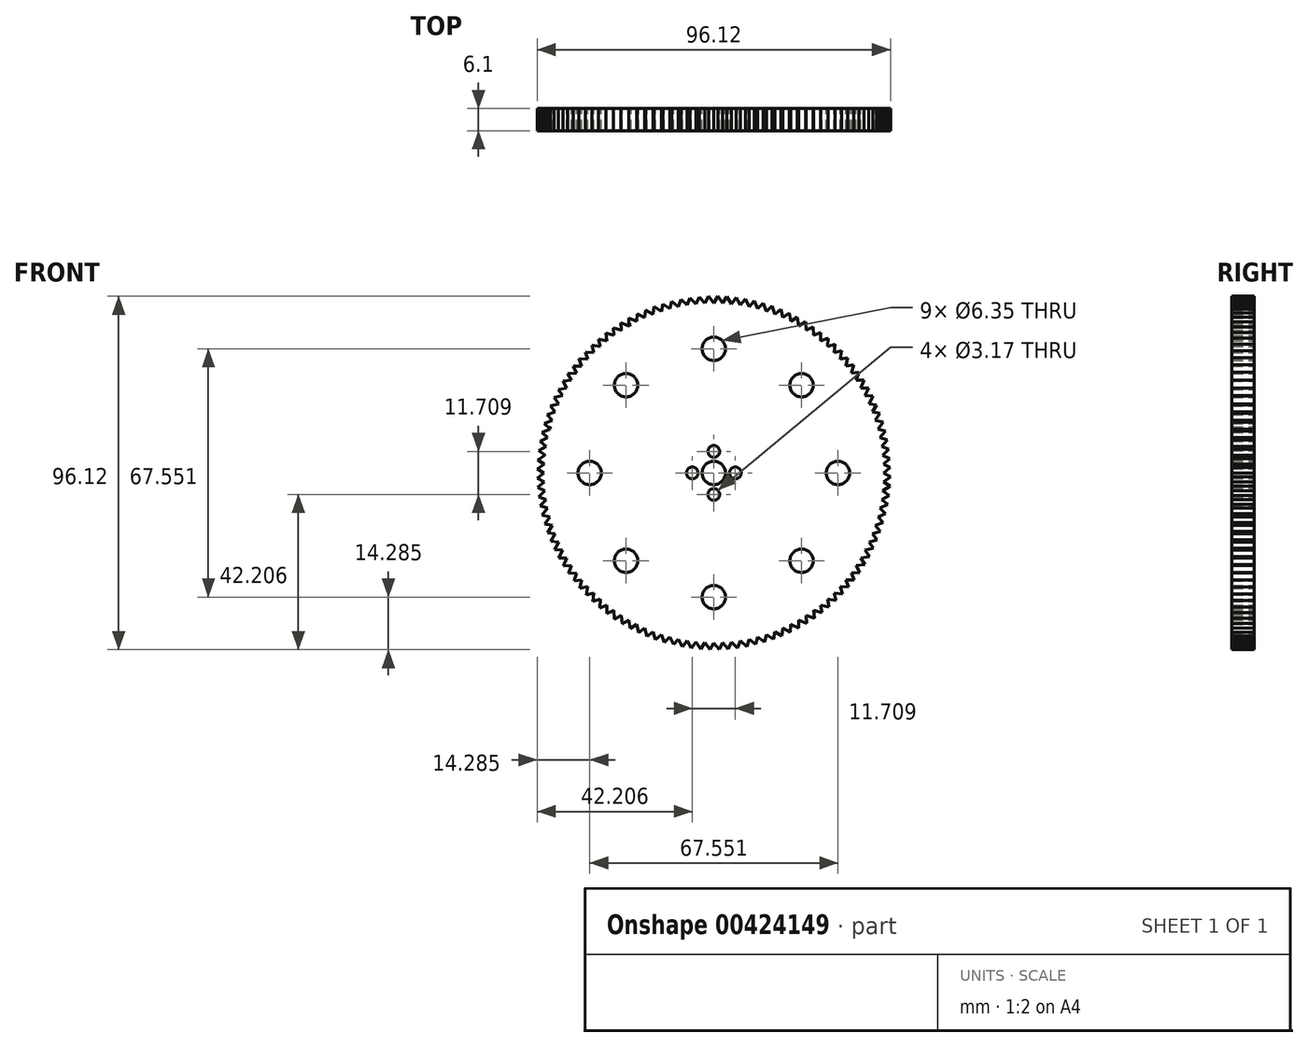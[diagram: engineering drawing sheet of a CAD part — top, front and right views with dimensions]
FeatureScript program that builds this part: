
annotation { "Feature Type Name" : "Feature", "Feature Type Description" : "" }
export const myFeature = defineFeature(function(context is Context, id is Id, definition is map)
    precondition{}
    {
        {
            var Q0;
            Q0=qCreatedBy(makeId("Front.planeOp"),FACE);
            var sketch = newSketch(context, id + "F0", { "sketchPlane" : qUnion([Q0])});
            skCircle(sketch, "E0", {"center": v(0, 0) * mm, "radius": 46.23 * mm});
            skPoint(sketch, "E1", {"position": v(0, 33.78) * mm});
            skPoint(sketch, "E2.1.0", {"position": v(23.88, 23.88) * mm});
            skPoint(sketch, "E2.2.0", {"position": v(33.78, 0) * mm});
            skPoint(sketch, "E2.3.0", {"position": v(23.88, -23.88) * mm});
            skPoint(sketch, "E2.4.0", {"position": v(0, -33.78) * mm});
            skPoint(sketch, "E2.5.0", {"position": v(-23.88, -23.88) * mm});
            skPoint(sketch, "E2.6.0", {"position": v(-33.78, 0) * mm});
            skPoint(sketch, "E2.7.0", {"position": v(-23.88, 23.88) * mm});
            skLineSegment(sketch, "E2.anchor1", {"start": v(0, 0) * mm, "end": v(0, 33.78) * mm, "construction": true});
            skLineSegment(sketch, "E2.anchor2", {"start": v(0, 0) * mm, "end": v(-23.88, 23.88) * mm, "construction": true});
            skPoint(sketch, "E3", {"position": v(0, -5.85) * mm});
            skPoint(sketch, "E4.1.0", {"position": v(-5.85, 0) * mm});
            skPoint(sketch, "E4.2.0", {"position": v(0, 5.85) * mm});
            skPoint(sketch, "E4.3.0", {"position": v(5.85, 0) * mm});
            skLineSegment(sketch, "E4.anchor1", {"start": v(0, 0) * mm, "end": v(0, -5.85) * mm, "construction": true});
            skLineSegment(sketch, "E4.anchor2", {"start": v(0, 0) * mm, "end": v(5.85, 0) * mm, "construction": true});
            skPoint(sketch, "E5", {"position": v(0, -46.23) * mm});
            skPoint(sketch, "E6.1.0", {"position": v(2.42, -46.16) * mm});
            skPoint(sketch, "E6.2.0", {"position": v(4.83, -45.97) * mm});
            skPoint(sketch, "E6.3.0", {"position": v(7.23, -45.66) * mm});
            skPoint(sketch, "E6.4.0", {"position": v(9.61, -45.22) * mm});
            skPoint(sketch, "E6.5.0", {"position": v(11.96, -44.65) * mm});
            skPoint(sketch, "E6.6.0", {"position": v(14.29, -43.97) * mm});
            skPoint(sketch, "E6.7.0", {"position": v(16.57, -43.16) * mm});
            skPoint(sketch, "E6.8.0", {"position": v(18.8, -42.23) * mm});
            skPoint(sketch, "E6.9.0", {"position": v(20.99, -41.19) * mm});
            skPoint(sketch, "E6.10.0", {"position": v(23.11, -40.03) * mm});
            skPoint(sketch, "E6.11.0", {"position": v(25.18, -38.77) * mm});
            skPoint(sketch, "E6.12.0", {"position": v(27.17, -37.4) * mm});
            skPoint(sketch, "E6.13.0", {"position": v(29.1, -35.93) * mm});
            skPoint(sketch, "E6.14.0", {"position": v(30.93, -34.35) * mm});
            skPoint(sketch, "E6.15.0", {"position": v(32.69, -32.69) * mm});
            skPoint(sketch, "E6.16.0", {"position": v(34.35, -30.93) * mm});
            skPoint(sketch, "E6.17.0", {"position": v(35.93, -29.1) * mm});
            skPoint(sketch, "E6.18.0", {"position": v(37.4, -27.17) * mm});
            skPoint(sketch, "E6.19.0", {"position": v(38.77, -25.18) * mm});
            skPoint(sketch, "E6.20.0", {"position": v(40.03, -23.11) * mm});
            skPoint(sketch, "E6.21.0", {"position": v(41.19, -20.99) * mm});
            skPoint(sketch, "E6.22.0", {"position": v(42.23, -18.8) * mm});
            skPoint(sketch, "E6.23.0", {"position": v(43.16, -16.57) * mm});
            skPoint(sketch, "E6.24.0", {"position": v(43.97, -14.29) * mm});
            skPoint(sketch, "E6.25.0", {"position": v(44.65, -11.96) * mm});
            skPoint(sketch, "E6.26.0", {"position": v(45.22, -9.61) * mm});
            skPoint(sketch, "E6.27.0", {"position": v(45.66, -7.23) * mm});
            skPoint(sketch, "E6.28.0", {"position": v(45.97, -4.83) * mm});
            skPoint(sketch, "E6.29.0", {"position": v(46.16, -2.42) * mm});
            skPoint(sketch, "E6.30.0", {"position": v(46.23, 0) * mm});
            skPoint(sketch, "E6.31.0", {"position": v(46.16, 2.42) * mm});
            skPoint(sketch, "E6.32.0", {"position": v(45.97, 4.83) * mm});
            skPoint(sketch, "E6.33.0", {"position": v(45.66, 7.23) * mm});
            skPoint(sketch, "E6.34.0", {"position": v(45.22, 9.61) * mm});
            skPoint(sketch, "E6.35.0", {"position": v(44.65, 11.96) * mm});
            skPoint(sketch, "E6.36.0", {"position": v(43.97, 14.29) * mm});
            skPoint(sketch, "E6.37.0", {"position": v(43.16, 16.57) * mm});
            skPoint(sketch, "E6.38.0", {"position": v(42.23, 18.8) * mm});
            skPoint(sketch, "E6.39.0", {"position": v(41.19, 20.99) * mm});
            skPoint(sketch, "E6.40.0", {"position": v(40.03, 23.11) * mm});
            skPoint(sketch, "E6.41.0", {"position": v(38.77, 25.18) * mm});
            skPoint(sketch, "E6.42.0", {"position": v(37.4, 27.17) * mm});
            skPoint(sketch, "E6.43.0", {"position": v(35.93, 29.1) * mm});
            skPoint(sketch, "E6.44.0", {"position": v(34.35, 30.93) * mm});
            skPoint(sketch, "E6.45.0", {"position": v(32.69, 32.69) * mm});
            skPoint(sketch, "E6.46.0", {"position": v(30.93, 34.35) * mm});
            skPoint(sketch, "E6.47.0", {"position": v(29.1, 35.93) * mm});
            skPoint(sketch, "E6.48.0", {"position": v(27.17, 37.4) * mm});
            skPoint(sketch, "E6.49.0", {"position": v(25.18, 38.77) * mm});
            skPoint(sketch, "E6.50.0", {"position": v(23.11, 40.03) * mm});
            skPoint(sketch, "E6.51.0", {"position": v(20.99, 41.19) * mm});
            skPoint(sketch, "E6.52.0", {"position": v(18.8, 42.23) * mm});
            skPoint(sketch, "E6.53.0", {"position": v(16.57, 43.16) * mm});
            skPoint(sketch, "E6.54.0", {"position": v(14.29, 43.97) * mm});
            skPoint(sketch, "E6.55.0", {"position": v(11.96, 44.65) * mm});
            skPoint(sketch, "E6.56.0", {"position": v(9.61, 45.22) * mm});
            skPoint(sketch, "E6.57.0", {"position": v(7.23, 45.66) * mm});
            skPoint(sketch, "E6.58.0", {"position": v(4.83, 45.97) * mm});
            skPoint(sketch, "E6.59.0", {"position": v(2.42, 46.16) * mm});
            skPoint(sketch, "E6.60.0", {"position": v(0, 46.23) * mm});
            skPoint(sketch, "E6.61.0", {"position": v(-2.42, 46.16) * mm});
            skPoint(sketch, "E6.62.0", {"position": v(-4.83, 45.97) * mm});
            skPoint(sketch, "E6.63.0", {"position": v(-7.23, 45.66) * mm});
            skPoint(sketch, "E6.64.0", {"position": v(-9.61, 45.22) * mm});
            skPoint(sketch, "E6.65.0", {"position": v(-11.96, 44.65) * mm});
            skPoint(sketch, "E6.66.0", {"position": v(-14.29, 43.97) * mm});
            skPoint(sketch, "E6.67.0", {"position": v(-16.57, 43.16) * mm});
            skPoint(sketch, "E6.68.0", {"position": v(-18.8, 42.23) * mm});
            skPoint(sketch, "E6.69.0", {"position": v(-20.99, 41.19) * mm});
            skPoint(sketch, "E6.70.0", {"position": v(-23.11, 40.03) * mm});
            skPoint(sketch, "E6.71.0", {"position": v(-25.18, 38.77) * mm});
            skPoint(sketch, "E6.72.0", {"position": v(-27.17, 37.4) * mm});
            skPoint(sketch, "E6.73.0", {"position": v(-29.1, 35.93) * mm});
            skPoint(sketch, "E6.74.0", {"position": v(-30.93, 34.35) * mm});
            skPoint(sketch, "E6.75.0", {"position": v(-32.69, 32.69) * mm});
            skPoint(sketch, "E6.76.0", {"position": v(-34.35, 30.93) * mm});
            skPoint(sketch, "E6.77.0", {"position": v(-35.93, 29.1) * mm});
            skPoint(sketch, "E6.78.0", {"position": v(-37.4, 27.17) * mm});
            skPoint(sketch, "E6.79.0", {"position": v(-38.77, 25.18) * mm});
            skPoint(sketch, "E6.80.0", {"position": v(-40.03, 23.11) * mm});
            skPoint(sketch, "E6.81.0", {"position": v(-41.19, 20.99) * mm});
            skPoint(sketch, "E6.82.0", {"position": v(-42.23, 18.8) * mm});
            skPoint(sketch, "E6.83.0", {"position": v(-43.16, 16.57) * mm});
            skPoint(sketch, "E6.84.0", {"position": v(-43.97, 14.29) * mm});
            skPoint(sketch, "E6.85.0", {"position": v(-44.65, 11.96) * mm});
            skPoint(sketch, "E6.86.0", {"position": v(-45.22, 9.61) * mm});
            skPoint(sketch, "E6.87.0", {"position": v(-45.66, 7.23) * mm});
            skPoint(sketch, "E6.88.0", {"position": v(-45.97, 4.83) * mm});
            skPoint(sketch, "E6.89.0", {"position": v(-46.16, 2.42) * mm});
            skPoint(sketch, "E6.90.0", {"position": v(-46.23, 0) * mm});
            skPoint(sketch, "E6.91.0", {"position": v(-46.16, -2.42) * mm});
            skPoint(sketch, "E6.92.0", {"position": v(-45.97, -4.83) * mm});
            skPoint(sketch, "E6.93.0", {"position": v(-45.66, -7.23) * mm});
            skPoint(sketch, "E6.94.0", {"position": v(-45.22, -9.61) * mm});
            skPoint(sketch, "E6.95.0", {"position": v(-44.65, -11.96) * mm});
            skPoint(sketch, "E6.96.0", {"position": v(-43.97, -14.29) * mm});
            skPoint(sketch, "E6.97.0", {"position": v(-43.16, -16.57) * mm});
            skPoint(sketch, "E6.98.0", {"position": v(-42.23, -18.8) * mm});
            skPoint(sketch, "E6.99.0", {"position": v(-41.19, -20.99) * mm});
            skPoint(sketch, "E6.100.0", {"position": v(-40.03, -23.11) * mm});
            skPoint(sketch, "E6.101.0", {"position": v(-38.77, -25.18) * mm});
            skPoint(sketch, "E6.102.0", {"position": v(-37.4, -27.17) * mm});
            skPoint(sketch, "E6.103.0", {"position": v(-35.93, -29.1) * mm});
            skPoint(sketch, "E6.104.0", {"position": v(-34.35, -30.93) * mm});
            skPoint(sketch, "E6.105.0", {"position": v(-32.69, -32.69) * mm});
            skPoint(sketch, "E6.106.0", {"position": v(-30.93, -34.35) * mm});
            skPoint(sketch, "E6.107.0", {"position": v(-29.1, -35.93) * mm});
            skPoint(sketch, "E6.108.0", {"position": v(-27.17, -37.4) * mm});
            skPoint(sketch, "E6.109.0", {"position": v(-25.18, -38.77) * mm});
            skPoint(sketch, "E6.110.0", {"position": v(-23.11, -40.03) * mm});
            skPoint(sketch, "E6.111.0", {"position": v(-20.99, -41.19) * mm});
            skPoint(sketch, "E6.112.0", {"position": v(-18.8, -42.23) * mm});
            skPoint(sketch, "E6.113.0", {"position": v(-16.57, -43.16) * mm});
            skPoint(sketch, "E6.114.0", {"position": v(-14.29, -43.97) * mm});
            skPoint(sketch, "E6.115.0", {"position": v(-11.96, -44.65) * mm});
            skPoint(sketch, "E6.116.0", {"position": v(-9.61, -45.22) * mm});
            skPoint(sketch, "E6.117.0", {"position": v(-7.23, -45.66) * mm});
            skPoint(sketch, "E6.118.0", {"position": v(-4.83, -45.97) * mm});
            skPoint(sketch, "E6.119.0", {"position": v(-2.42, -46.16) * mm});
            skPoint(sketch, "E7", {"position": v(1.45, -48.05) * mm});
            skPoint(sketch, "E8.1.0", {"position": v(3.96, -47.9) * mm});
            skPoint(sketch, "E8.2.0", {"position": v(6.46, -47.63) * mm});
            skPoint(sketch, "E8.3.0", {"position": v(8.95, -47.23) * mm});
            skPoint(sketch, "E8.4.0", {"position": v(11.4, -46.7) * mm});
            skPoint(sketch, "E8.5.0", {"position": v(13.84, -46.03) * mm});
            skPoint(sketch, "E8.6.0", {"position": v(16.23, -45.25) * mm});
            skPoint(sketch, "E8.7.0", {"position": v(18.57, -44.34) * mm});
            skPoint(sketch, "E8.8.0", {"position": v(20.87, -43.3) * mm});
            skPoint(sketch, "E8.9.0", {"position": v(23.1, -42.15) * mm});
            skPoint(sketch, "E8.10.0", {"position": v(25.28, -40.88) * mm});
            skPoint(sketch, "E8.11.0", {"position": v(27.38, -39.5) * mm});
            skPoint(sketch, "E8.12.0", {"position": v(29.41, -38.02) * mm});
            skPoint(sketch, "E8.13.0", {"position": v(31.36, -36.43) * mm});
            skPoint(sketch, "E8.14.0", {"position": v(33.23, -34.74) * mm});
            skPoint(sketch, "E8.15.0", {"position": v(35, -32.95) * mm});
            skPoint(sketch, "E8.16.0", {"position": v(36.68, -31.07) * mm});
            skPoint(sketch, "E8.17.0", {"position": v(38.25, -29.1) * mm});
            skPoint(sketch, "E8.18.0", {"position": v(39.72, -27.07) * mm});
            skPoint(sketch, "E8.19.0", {"position": v(41.08, -24.95) * mm});
            skPoint(sketch, "E8.20.0", {"position": v(42.33, -22.77) * mm});
            skPoint(sketch, "E8.21.0", {"position": v(43.47, -20.52) * mm});
            skPoint(sketch, "E8.22.0", {"position": v(44.48, -18.22) * mm});
            skPoint(sketch, "E8.23.0", {"position": v(45.37, -15.86) * mm});
            skPoint(sketch, "E8.24.0", {"position": v(46.14, -13.47) * mm});
            skPoint(sketch, "E8.25.0", {"position": v(46.78, -11.04) * mm});
            skPoint(sketch, "E8.26.0", {"position": v(47.3, -8.57) * mm});
            skPoint(sketch, "E8.27.0", {"position": v(47.68, -6.08) * mm});
            skPoint(sketch, "E8.28.0", {"position": v(47.93, -3.58) * mm});
            skPoint(sketch, "E8.29.0", {"position": v(48.06, -1.07) * mm});
            skPoint(sketch, "E8.30.0", {"position": v(48.05, 1.45) * mm});
            skPoint(sketch, "E8.31.0", {"position": v(47.9, 3.96) * mm});
            skPoint(sketch, "E8.32.0", {"position": v(47.63, 6.46) * mm});
            skPoint(sketch, "E8.33.0", {"position": v(47.23, 8.95) * mm});
            skPoint(sketch, "E8.34.0", {"position": v(46.7, 11.4) * mm});
            skPoint(sketch, "E8.35.0", {"position": v(46.03, 13.84) * mm});
            skPoint(sketch, "E8.36.0", {"position": v(45.25, 16.23) * mm});
            skPoint(sketch, "E8.37.0", {"position": v(44.34, 18.57) * mm});
            skPoint(sketch, "E8.38.0", {"position": v(43.3, 20.87) * mm});
            skPoint(sketch, "E8.39.0", {"position": v(42.15, 23.1) * mm});
            skPoint(sketch, "E8.40.0", {"position": v(40.88, 25.28) * mm});
            skPoint(sketch, "E8.41.0", {"position": v(39.5, 27.38) * mm});
            skPoint(sketch, "E8.42.0", {"position": v(38.02, 29.41) * mm});
            skPoint(sketch, "E8.43.0", {"position": v(36.43, 31.36) * mm});
            skPoint(sketch, "E8.44.0", {"position": v(34.74, 33.23) * mm});
            skPoint(sketch, "E8.45.0", {"position": v(32.95, 35) * mm});
            skPoint(sketch, "E8.46.0", {"position": v(31.07, 36.68) * mm});
            skPoint(sketch, "E8.47.0", {"position": v(29.1, 38.25) * mm});
            skPoint(sketch, "E8.48.0", {"position": v(27.07, 39.72) * mm});
            skPoint(sketch, "E8.49.0", {"position": v(24.95, 41.08) * mm});
            skPoint(sketch, "E8.50.0", {"position": v(22.77, 42.33) * mm});
            skPoint(sketch, "E8.51.0", {"position": v(20.52, 43.47) * mm});
            skPoint(sketch, "E8.52.0", {"position": v(18.22, 44.48) * mm});
            skPoint(sketch, "E8.53.0", {"position": v(15.86, 45.37) * mm});
            skPoint(sketch, "E8.54.0", {"position": v(13.47, 46.14) * mm});
            skPoint(sketch, "E8.55.0", {"position": v(11.04, 46.78) * mm});
            skPoint(sketch, "E8.56.0", {"position": v(8.57, 47.3) * mm});
            skPoint(sketch, "E8.57.0", {"position": v(6.08, 47.68) * mm});
            skPoint(sketch, "E8.58.0", {"position": v(3.58, 47.93) * mm});
            skPoint(sketch, "E8.59.0", {"position": v(1.07, 48.06) * mm});
            skPoint(sketch, "E8.60.0", {"position": v(-1.45, 48.05) * mm});
            skPoint(sketch, "E8.61.0", {"position": v(-3.96, 47.9) * mm});
            skPoint(sketch, "E8.62.0", {"position": v(-6.46, 47.63) * mm});
            skPoint(sketch, "E8.63.0", {"position": v(-8.95, 47.23) * mm});
            skPoint(sketch, "E8.64.0", {"position": v(-11.4, 46.7) * mm});
            skPoint(sketch, "E8.65.0", {"position": v(-13.84, 46.03) * mm});
            skPoint(sketch, "E8.66.0", {"position": v(-16.23, 45.25) * mm});
            skPoint(sketch, "E8.67.0", {"position": v(-18.57, 44.34) * mm});
            skPoint(sketch, "E8.68.0", {"position": v(-20.87, 43.3) * mm});
            skPoint(sketch, "E8.69.0", {"position": v(-23.1, 42.15) * mm});
            skPoint(sketch, "E8.70.0", {"position": v(-25.28, 40.88) * mm});
            skPoint(sketch, "E8.71.0", {"position": v(-27.38, 39.5) * mm});
            skPoint(sketch, "E8.72.0", {"position": v(-29.41, 38.02) * mm});
            skPoint(sketch, "E8.73.0", {"position": v(-31.36, 36.43) * mm});
            skPoint(sketch, "E8.74.0", {"position": v(-33.23, 34.74) * mm});
            skPoint(sketch, "E8.75.0", {"position": v(-35, 32.95) * mm});
            skPoint(sketch, "E8.76.0", {"position": v(-36.68, 31.07) * mm});
            skPoint(sketch, "E8.77.0", {"position": v(-38.25, 29.1) * mm});
            skPoint(sketch, "E8.78.0", {"position": v(-39.72, 27.07) * mm});
            skPoint(sketch, "E8.79.0", {"position": v(-41.08, 24.95) * mm});
            skPoint(sketch, "E8.80.0", {"position": v(-42.33, 22.77) * mm});
            skPoint(sketch, "E8.81.0", {"position": v(-43.47, 20.52) * mm});
            skPoint(sketch, "E8.82.0", {"position": v(-44.48, 18.22) * mm});
            skPoint(sketch, "E8.83.0", {"position": v(-45.37, 15.86) * mm});
            skPoint(sketch, "E8.84.0", {"position": v(-46.14, 13.47) * mm});
            skPoint(sketch, "E8.85.0", {"position": v(-46.78, 11.04) * mm});
            skPoint(sketch, "E8.86.0", {"position": v(-47.3, 8.57) * mm});
            skPoint(sketch, "E8.87.0", {"position": v(-47.68, 6.08) * mm});
            skPoint(sketch, "E8.88.0", {"position": v(-47.93, 3.58) * mm});
            skPoint(sketch, "E8.89.0", {"position": v(-48.06, 1.07) * mm});
            skPoint(sketch, "E8.90.0", {"position": v(-48.05, -1.45) * mm});
            skPoint(sketch, "E8.91.0", {"position": v(-47.9, -3.96) * mm});
            skPoint(sketch, "E8.92.0", {"position": v(-47.63, -6.46) * mm});
            skPoint(sketch, "E8.93.0", {"position": v(-47.23, -8.95) * mm});
            skPoint(sketch, "E8.94.0", {"position": v(-46.7, -11.4) * mm});
            skPoint(sketch, "E8.95.0", {"position": v(-46.03, -13.84) * mm});
            skPoint(sketch, "E8.96.0", {"position": v(-45.25, -16.23) * mm});
            skPoint(sketch, "E8.97.0", {"position": v(-44.34, -18.57) * mm});
            skPoint(sketch, "E8.98.0", {"position": v(-43.3, -20.87) * mm});
            skPoint(sketch, "E8.99.0", {"position": v(-42.15, -23.1) * mm});
            skPoint(sketch, "E8.100.0", {"position": v(-40.88, -25.28) * mm});
            skPoint(sketch, "E8.101.0", {"position": v(-39.5, -27.38) * mm});
            skPoint(sketch, "E8.102.0", {"position": v(-38.02, -29.41) * mm});
            skPoint(sketch, "E8.103.0", {"position": v(-36.43, -31.36) * mm});
            skPoint(sketch, "E8.104.0", {"position": v(-34.74, -33.23) * mm});
            skPoint(sketch, "E8.105.0", {"position": v(-32.95, -35) * mm});
            skPoint(sketch, "E8.106.0", {"position": v(-31.07, -36.68) * mm});
            skPoint(sketch, "E8.107.0", {"position": v(-29.1, -38.25) * mm});
            skPoint(sketch, "E8.108.0", {"position": v(-27.07, -39.72) * mm});
            skPoint(sketch, "E8.109.0", {"position": v(-24.95, -41.08) * mm});
            skPoint(sketch, "E8.110.0", {"position": v(-22.77, -42.33) * mm});
            skPoint(sketch, "E8.111.0", {"position": v(-20.52, -43.47) * mm});
            skPoint(sketch, "E8.112.0", {"position": v(-18.22, -44.48) * mm});
            skPoint(sketch, "E8.113.0", {"position": v(-15.86, -45.37) * mm});
            skPoint(sketch, "E8.114.0", {"position": v(-13.47, -46.14) * mm});
            skPoint(sketch, "E8.115.0", {"position": v(-11.04, -46.78) * mm});
            skPoint(sketch, "E8.116.0", {"position": v(-8.57, -47.3) * mm});
            skPoint(sketch, "E8.117.0", {"position": v(-6.08, -47.68) * mm});
            skPoint(sketch, "E8.118.0", {"position": v(-3.58, -47.93) * mm});
            skPoint(sketch, "E8.119.0", {"position": v(-1.07, -48.06) * mm});
            skLineSegment(sketch, "E9", {"start": v(-1.07, -48.06) * mm, "end": v(0, -46.23) * mm});
            skLineSegment(sketch, "E10", {"start": v(0, -46.23) * mm, "end": v(1.45, -48.05) * mm});
            skLineSegment(sketch, "E11", {"start": v(1.47, -48.03) * mm, "end": v(2.42, -46.16) * mm});
            skLineSegment(sketch, "E12", {"start": v(2.42, -46.16) * mm, "end": v(3.96, -47.9) * mm});
            skLineSegment(sketch, "E13", {"start": v(4.83, -45.97) * mm, "end": v(3.96, -47.9) * mm});
            skLineSegment(sketch, "E14", {"start": v(-1.07, -48.06) * mm, "end": v(-2.42, -46.16) * mm});
            skLineSegment(sketch, "E15", {"start": v(0, -46.23) * mm, "end": v(1.47, -48.03) * mm});
            skLineSegment(sketch, "E16", {"start": v(4.83, -45.97) * mm, "end": v(6.46, -47.63) * mm});
            skLineSegment(sketch, "E17", {"start": v(6.46, -47.63) * mm, "end": v(7.23, -45.66) * mm});
            skLineSegment(sketch, "E18", {"start": v(-2.42, -46.16) * mm, "end": v(-3.58, -47.93) * mm});
            skLineSegment(sketch, "E19", {"start": v(-3.58, -47.93) * mm, "end": v(-4.83, -45.97) * mm});
            skLineSegment(sketch, "E20", {"start": v(-4.83, -45.97) * mm, "end": v(-6.08, -47.68) * mm});
            skLineSegment(sketch, "E21", {"start": v(-6.08, -47.68) * mm, "end": v(-7.23, -45.66) * mm});
            skLineSegment(sketch, "E22", {"start": v(-8.57, -47.3) * mm, "end": v(-7.23, -45.66) * mm});
            skLineSegment(sketch, "E23", {"start": v(-8.64, -47.4) * mm, "end": v(-9.61, -45.22) * mm});
            skLineSegment(sketch, "E24", {"start": v(-9.61, -45.22) * mm, "end": v(-11.04, -46.78) * mm});
            skLineSegment(sketch, "E25", {"start": v(-10.94, -46.71) * mm, "end": v(-11.96, -44.65) * mm});
            skLineSegment(sketch, "E26", {"start": v(-9.61, -45.22) * mm, "end": v(-8.57, -47.3) * mm});
            skLineSegment(sketch, "E27", {"start": v(-14.29, -43.97) * mm, "end": v(-13.47, -46.14) * mm});
            skLineSegment(sketch, "E28", {"start": v(-11.96, -44.65) * mm, "end": v(-13.47, -46.14) * mm});
            skLineSegment(sketch, "E29", {"start": v(-14.29, -43.97) * mm, "end": v(-15.86, -45.37) * mm});
            skLineSegment(sketch, "E30", {"start": v(-30.93, -34.35) * mm, "end": v(-31.07, -36.68) * mm});
            skLineSegment(sketch, "E31", {"start": v(-31.07, -36.68) * mm, "end": v(-29.1, -35.93) * mm});
            skLineSegment(sketch, "E32", {"start": v(-29.1, -35.93) * mm, "end": v(-29.1, -38.25) * mm});
            skLineSegment(sketch, "E33", {"start": v(-29.1, -38.25) * mm, "end": v(-27.17, -37.4) * mm});
            skLineSegment(sketch, "E34", {"start": v(-27.17, -37.4) * mm, "end": v(-27.07, -39.72) * mm});
            skLineSegment(sketch, "E35", {"start": v(-27.07, -39.72) * mm, "end": v(-25.18, -38.77) * mm});
            skLineSegment(sketch, "E36", {"start": v(-25.18, -38.77) * mm, "end": v(-24.95, -41.08) * mm});
            skLineSegment(sketch, "E37", {"start": v(-24.95, -41.08) * mm, "end": v(-23.11, -40.03) * mm});
            skLineSegment(sketch, "E38", {"start": v(-23.11, -40.03) * mm, "end": v(-22.77, -42.33) * mm});
            skLineSegment(sketch, "E39", {"start": v(-22.77, -42.33) * mm, "end": v(-20.99, -41.19) * mm});
            skLineSegment(sketch, "E40", {"start": v(-20.99, -41.19) * mm, "end": v(-20.52, -43.47) * mm});
            skLineSegment(sketch, "E41", {"start": v(-20.52, -43.47) * mm, "end": v(-18.8, -42.23) * mm});
            skLineSegment(sketch, "E42", {"start": v(-18.8, -42.23) * mm, "end": v(-18.22, -44.48) * mm});
            skLineSegment(sketch, "E43", {"start": v(-18.22, -44.48) * mm, "end": v(-16.57, -43.16) * mm});
            skLineSegment(sketch, "E44", {"start": v(-16.57, -43.16) * mm, "end": v(-15.86, -45.37) * mm});
            skLineSegment(sketch, "E45", {"start": v(7.23, -45.66) * mm, "end": v(8.95, -47.23) * mm});
            skLineSegment(sketch, "E46", {"start": v(8.95, -47.23) * mm, "end": v(9.61, -45.22) * mm});
            skLineSegment(sketch, "E47", {"start": v(9.61, -45.22) * mm, "end": v(11.4, -46.7) * mm});
            skLineSegment(sketch, "E48", {"start": v(11.4, -46.7) * mm, "end": v(11.96, -44.65) * mm});
            skLineSegment(sketch, "E49", {"start": v(11.96, -44.65) * mm, "end": v(13.84, -46.03) * mm});
            skLineSegment(sketch, "E50", {"start": v(13.84, -46.03) * mm, "end": v(14.29, -43.97) * mm});
            skLineSegment(sketch, "E51", {"start": v(14.29, -43.97) * mm, "end": v(16.23, -45.25) * mm});
            skLineSegment(sketch, "E52", {"start": v(16.23, -45.25) * mm, "end": v(16.57, -43.16) * mm});
            skLineSegment(sketch, "E53", {"start": v(16.57, -43.16) * mm, "end": v(18.57, -44.34) * mm});
            skLineSegment(sketch, "E54", {"start": v(18.57, -44.34) * mm, "end": v(18.8, -42.23) * mm});
            skLineSegment(sketch, "E55", {"start": v(18.8, -42.23) * mm, "end": v(20.87, -43.3) * mm});
            skLineSegment(sketch, "E56", {"start": v(20.87, -43.3) * mm, "end": v(20.99, -41.19) * mm});
            skLineSegment(sketch, "E57", {"start": v(20.99, -41.19) * mm, "end": v(23.1, -42.15) * mm});
            skLineSegment(sketch, "E58", {"start": v(23.1, -42.15) * mm, "end": v(23.11, -40.03) * mm});
            skLineSegment(sketch, "E59", {"start": v(23.11, -40.03) * mm, "end": v(25.28, -40.88) * mm});
            skLineSegment(sketch, "E60", {"start": v(25.28, -40.88) * mm, "end": v(25.18, -38.77) * mm});
            skLineSegment(sketch, "E61", {"start": v(25.18, -38.77) * mm, "end": v(27.38, -39.5) * mm});
            skLineSegment(sketch, "E62", {"start": v(27.38, -39.5) * mm, "end": v(27.17, -37.4) * mm});
            skLineSegment(sketch, "E63", {"start": v(27.17, -37.4) * mm, "end": v(29.41, -38.02) * mm});
            skLineSegment(sketch, "E64", {"start": v(29.41, -38.02) * mm, "end": v(29.1, -35.93) * mm});
            skLineSegment(sketch, "E65", {"start": v(29.1, -35.93) * mm, "end": v(31.36, -36.43) * mm});
            skLineSegment(sketch, "E66", {"start": v(31.36, -36.43) * mm, "end": v(30.93, -34.35) * mm});
            skLineSegment(sketch, "E67", {"start": v(30.93, -34.35) * mm, "end": v(33.23, -34.74) * mm});
            skLineSegment(sketch, "E68", {"start": v(33.23, -34.74) * mm, "end": v(32.69, -32.69) * mm});
            skLineSegment(sketch, "E69", {"start": v(32.69, -32.69) * mm, "end": v(35, -32.95) * mm});
            skLineSegment(sketch, "E70", {"start": v(35, -32.95) * mm, "end": v(34.35, -30.93) * mm});
            skLineSegment(sketch, "E71", {"start": v(34.35, -30.93) * mm, "end": v(36.68, -31.07) * mm});
            skLineSegment(sketch, "E72", {"start": v(36.68, -31.07) * mm, "end": v(35.93, -29.1) * mm});
            skLineSegment(sketch, "E73", {"start": v(35.93, -29.1) * mm, "end": v(38.25, -29.1) * mm});
            skLineSegment(sketch, "E74", {"start": v(-32.69, -32.69) * mm, "end": v(-32.95, -35) * mm});
            skLineSegment(sketch, "E75", {"start": v(-30.93, -34.35) * mm, "end": v(-32.95, -35) * mm});
            skLineSegment(sketch, "E76", {"start": v(-34.74, -33.23) * mm, "end": v(-32.69, -32.69) * mm});
            skLineSegment(sketch, "E77", {"start": v(-34.74, -33.23) * mm, "end": v(-34.35, -30.93) * mm});
            skLineSegment(sketch, "E78", {"start": v(-34.35, -30.93) * mm, "end": v(-36.43, -31.36) * mm});
            skLineSegment(sketch, "E79", {"start": v(-36.43, -31.36) * mm, "end": v(-35.93, -29.1) * mm});
            skLineSegment(sketch, "E80", {"start": v(-37.4, -27.17) * mm, "end": v(-38.02, -29.41) * mm});
            skLineSegment(sketch, "E81", {"start": v(-38.02, -29.41) * mm, "end": v(-35.93, -29.1) * mm});
            skLineSegment(sketch, "E82", {"start": v(-39.5, -27.38) * mm, "end": v(-37.4, -27.17) * mm});
            skLineSegment(sketch, "E83", {"start": v(-39.5, -27.38) * mm, "end": v(-38.77, -25.18) * mm});
            skLineSegment(sketch, "E84", {"start": v(-38.77, -25.18) * mm, "end": v(-40.88, -25.28) * mm});
            skLineSegment(sketch, "E85", {"start": v(-40.88, -25.28) * mm, "end": v(-40.03, -23.11) * mm});
            skLineSegment(sketch, "E86", {"start": v(-40.03, -23.11) * mm, "end": v(-42.15, -23.1) * mm});
            skLineSegment(sketch, "E87", {"start": v(-42.15, -23.1) * mm, "end": v(-41.19, -20.99) * mm});
            skLineSegment(sketch, "E88", {"start": v(-41.19, -20.99) * mm, "end": v(-43.3, -20.87) * mm});
            skLineSegment(sketch, "E89", {"start": v(-43.3, -20.87) * mm, "end": v(-42.23, -18.8) * mm});
            skLineSegment(sketch, "E90", {"start": v(-42.23, -18.8) * mm, "end": v(-44.34, -18.57) * mm});
            skLineSegment(sketch, "E91", {"start": v(-44.34, -18.57) * mm, "end": v(-43.16, -16.57) * mm});
            skLineSegment(sketch, "E92", {"start": v(-43.16, -16.57) * mm, "end": v(-45.25, -16.23) * mm});
            skLineSegment(sketch, "E93", {"start": v(-45.25, -16.23) * mm, "end": v(-43.97, -14.29) * mm});
            skLineSegment(sketch, "E94", {"start": v(-43.97, -14.29) * mm, "end": v(-46.03, -13.84) * mm});
            skLineSegment(sketch, "E95", {"start": v(-46.03, -13.84) * mm, "end": v(-44.65, -11.96) * mm});
            skLineSegment(sketch, "E96", {"start": v(-44.65, -11.96) * mm, "end": v(-46.7, -11.4) * mm});
            skLineSegment(sketch, "E97", {"start": v(-46.7, -11.4) * mm, "end": v(-45.22, -9.61) * mm});
            skLineSegment(sketch, "E98", {"start": v(-45.22, -9.61) * mm, "end": v(-47.23, -8.95) * mm});
            skLineSegment(sketch, "E99", {"start": v(-47.23, -8.95) * mm, "end": v(-45.66, -7.23) * mm});
            skLineSegment(sketch, "E100", {"start": v(-45.66, -7.23) * mm, "end": v(-47.63, -6.46) * mm});
            skLineSegment(sketch, "E101", {"start": v(-47.63, -6.46) * mm, "end": v(-45.97, -4.83) * mm});
            skLineSegment(sketch, "E102", {"start": v(-45.92, -4.93) * mm, "end": v(-47.9, -3.96) * mm});
            skLineSegment(sketch, "E103", {"start": v(-47.89, -3.86) * mm, "end": v(-46.16, -2.42) * mm});
            skLineSegment(sketch, "E104", {"start": v(-46.16, -2.42) * mm, "end": v(-48.05, -1.45) * mm});
            skLineSegment(sketch, "E105", {"start": v(-48.05, -1.4) * mm, "end": v(-46.23, 0) * mm});
            skLineSegment(sketch, "E106", {"start": v(-46.23, 0) * mm, "end": v(-48.06, 1.07) * mm});
            skLineSegment(sketch, "E107", {"start": v(-48.06, 1.07) * mm, "end": v(-46.16, 2.42) * mm});
            skLineSegment(sketch, "E108", {"start": v(-46.16, 2.42) * mm, "end": v(-47.93, 3.58) * mm});
            skLineSegment(sketch, "E109", {"start": v(-47.93, 3.58) * mm, "end": v(-45.97, 4.83) * mm});
            skLineSegment(sketch, "E110", {"start": v(-45.92, 4.82) * mm, "end": v(-47.68, 6.08) * mm});
            skLineSegment(sketch, "E111", {"start": v(-47.89, -3.86) * mm, "end": v(-45.97, -4.83) * mm});
            skLineSegment(sketch, "E112", {"start": v(-47.9, -3.96) * mm, "end": v(-46.16, -2.42) * mm});
            skLineSegment(sketch, "E113", {"start": v(-48.17, -1.45) * mm, "end": v(-46.23, 0) * mm});
            skLineSegment(sketch, "E114", {"start": v(-46.23, 0) * mm, "end": v(-48.05, -1.45) * mm});
            skLineSegment(sketch, "E115", {"start": v(-47.68, 6.08) * mm, "end": v(-45.66, 7.23) * mm});
            skLineSegment(sketch, "E116", {"start": v(-45.66, 7.23) * mm, "end": v(-47.3, 8.57) * mm});
            skLineSegment(sketch, "E117", {"start": v(-47.3, 8.57) * mm, "end": v(-45.22, 9.61) * mm});
            skLineSegment(sketch, "E118", {"start": v(-45.15, 9.53) * mm, "end": v(-46.78, 11.04) * mm});
            skLineSegment(sketch, "E119", {"start": v(-46.78, 11.04) * mm, "end": v(-44.65, 11.96) * mm});
            skLineSegment(sketch, "E120", {"start": v(-44.65, 12.02) * mm, "end": v(-46.14, 13.47) * mm});
            skLineSegment(sketch, "E121", {"start": v(-46.14, 13.47) * mm, "end": v(-43.97, 14.29) * mm});
            skLineSegment(sketch, "E122", {"start": v(-46.14, 13.47) * mm, "end": v(-44.65, 12.02) * mm});
            skLineSegment(sketch, "E123", {"start": v(-44.65, 12.02) * mm, "end": v(-43.97, 14.29) * mm});
            skLineSegment(sketch, "E124", {"start": v(-43.97, 14.29) * mm, "end": v(-45.37, 15.86) * mm});
            skLineSegment(sketch, "E125", {"start": v(-45.37, 15.86) * mm, "end": v(-43.16, 16.57) * mm});
            skLineSegment(sketch, "E126", {"start": v(-43.16, 16.55) * mm, "end": v(-44.48, 18.22) * mm});
            skLineSegment(sketch, "E127", {"start": v(-44.48, 18.22) * mm, "end": v(-42.23, 18.8) * mm});
            skLineSegment(sketch, "E128", {"start": v(-42.23, 18.8) * mm, "end": v(-43.47, 20.52) * mm});
            skLineSegment(sketch, "E129", {"start": v(-43.47, 20.52) * mm, "end": v(-41.19, 20.99) * mm});
            skLineSegment(sketch, "E130", {"start": v(-41.19, 20.99) * mm, "end": v(-42.33, 22.77) * mm});
            skLineSegment(sketch, "E131", {"start": v(-42.39, 22.69) * mm, "end": v(-40.03, 23.11) * mm});
            skLineSegment(sketch, "E132", {"start": v(-40.03, 23.11) * mm, "end": v(-41.08, 24.95) * mm});
            skLineSegment(sketch, "E133", {"start": v(-41.08, 24.95) * mm, "end": v(-38.77, 25.18) * mm});
            skLineSegment(sketch, "E134", {"start": v(-38.77, 25.18) * mm, "end": v(-39.72, 27.07) * mm});
            skLineSegment(sketch, "E135", {"start": v(-39.72, 27.07) * mm, "end": v(-37.4, 27.17) * mm});
            skLineSegment(sketch, "E136", {"start": v(-37.4, 27.17) * mm, "end": v(-38.25, 29.1) * mm});
            skLineSegment(sketch, "E137", {"start": v(-38.34, 29.12) * mm, "end": v(-35.93, 29.1) * mm});
            skLineSegment(sketch, "E138", {"start": v(-38.25, 29.1) * mm, "end": v(-35.93, 29.1) * mm});
            skLineSegment(sketch, "E139", {"start": v(-35.93, 29.1) * mm, "end": v(-36.68, 31.07) * mm});
            skLineSegment(sketch, "E140", {"start": v(-36.68, 31.07) * mm, "end": v(-34.35, 30.93) * mm});
            skLineSegment(sketch, "E141", {"start": v(-34.35, 30.93) * mm, "end": v(-35, 32.95) * mm});
            skLineSegment(sketch, "E142", {"start": v(-35.02, 32.97) * mm, "end": v(-32.69, 32.69) * mm});
            skLineSegment(sketch, "E143", {"start": v(-32.69, 32.69) * mm, "end": v(-33.23, 34.74) * mm});
            skLineSegment(sketch, "E144", {"start": v(-33.23, 34.74) * mm, "end": v(-30.93, 34.35) * mm});
            skLineSegment(sketch, "E145", {"start": v(-30.98, 34.37) * mm, "end": v(-31.36, 36.43) * mm});
            skLineSegment(sketch, "E146", {"start": v(-31.36, 36.43) * mm, "end": v(-29.1, 35.93) * mm});
            skLineSegment(sketch, "E147", {"start": v(-34.96, 32.9) * mm, "end": v(-34.35, 30.93) * mm});
            skLineSegment(sketch, "E148", {"start": v(-34.96, 32.9) * mm, "end": v(-32.69, 32.69) * mm});
            skLineSegment(sketch, "E149", {"start": v(-30.93, 34.35) * mm, "end": v(-31.36, 36.43) * mm});
            skLineSegment(sketch, "E150", {"start": v(-29.1, 35.93) * mm, "end": v(-29.41, 38.02) * mm});
            skLineSegment(sketch, "E151", {"start": v(-29.41, 38.02) * mm, "end": v(-27.17, 37.4) * mm});
            skLineSegment(sketch, "E152", {"start": v(-27.26, 37.42) * mm, "end": v(-27.38, 39.5) * mm});
            skLineSegment(sketch, "E153", {"start": v(-27.38, 39.5) * mm, "end": v(-25.18, 38.77) * mm});
            skLineSegment(sketch, "E154", {"start": v(-25.13, 38.75) * mm, "end": v(-25.28, 40.88) * mm});
            skLineSegment(sketch, "E155", {"start": v(-25.28, 40.88) * mm, "end": v(-23.11, 40.03) * mm});
            skLineSegment(sketch, "E156", {"start": v(-23.08, 40.07) * mm, "end": v(-23.1, 42.15) * mm});
            skLineSegment(sketch, "E157", {"start": v(-23.1, 42.15) * mm, "end": v(-20.99, 41.19) * mm});
            skLineSegment(sketch, "E158", {"start": v(-23.08, 40.07) * mm, "end": v(-20.99, 41.19) * mm});
            skLineSegment(sketch, "E159", {"start": v(-20.99, 41.19) * mm, "end": v(-20.87, 43.3) * mm});
            skLineSegment(sketch, "E160", {"start": v(-18.85, 42.26) * mm, "end": v(-20.87, 43.3) * mm});
            skLineSegment(sketch, "E161", {"start": v(-18.8, 42.23) * mm, "end": v(-20.99, 41.19) * mm});
            skLineSegment(sketch, "E162", {"start": v(-18.8, 42.23) * mm, "end": v(-18.57, 44.34) * mm});
            skLineSegment(sketch, "E163", {"start": v(-16.57, 43.16) * mm, "end": v(-18.57, 44.34) * mm});
            skLineSegment(sketch, "E164", {"start": v(-18.8, 42.23) * mm, "end": v(-20.87, 43.3) * mm});
            skLineSegment(sketch, "E165", {"start": v(-16.57, 43.16) * mm, "end": v(-16.23, 45.25) * mm});
            skLineSegment(sketch, "E166", {"start": v(-16.22, 45.28) * mm, "end": v(-14.29, 43.97) * mm});
            skLineSegment(sketch, "E167", {"start": v(-14.3, 43.88) * mm, "end": v(-13.84, 46.03) * mm});
            skLineSegment(sketch, "E168", {"start": v(-13.9, 45.97) * mm, "end": v(-11.96, 44.65) * mm});
            skLineSegment(sketch, "E169", {"start": v(-12.05, 44.58) * mm, "end": v(-11.4, 46.7) * mm});
            skLineSegment(sketch, "E170", {"start": v(-11.43, 46.67) * mm, "end": v(-9.61, 45.22) * mm});
            skLineSegment(sketch, "E171", {"start": v(-16.57, 43.16) * mm, "end": v(-16.22, 45.28) * mm});
            skLineSegment(sketch, "E172", {"start": v(-9.61, 45.22) * mm, "end": v(-8.95, 47.23) * mm});
            skLineSegment(sketch, "E173", {"start": v(-8.96, 47.28) * mm, "end": v(-7.23, 45.66) * mm});
            skLineSegment(sketch, "E174", {"start": v(-7.23, 45.66) * mm, "end": v(-8.95, 47.23) * mm});
            skLineSegment(sketch, "E175", {"start": v(-7.23, 45.66) * mm, "end": v(-6.46, 47.63) * mm});
            skLineSegment(sketch, "E176", {"start": v(-6.49, 47.67) * mm, "end": v(-4.83, 45.97) * mm});
            skLineSegment(sketch, "E177", {"start": v(-4.83, 45.97) * mm, "end": v(-3.96, 47.9) * mm});
            skLineSegment(sketch, "E178", {"start": v(-4.83, 45.97) * mm, "end": v(-6.46, 47.63) * mm});
            skLineSegment(sketch, "E179", {"start": v(-3.96, 47.9) * mm, "end": v(-2.42, 46.16) * mm});
            skLineSegment(sketch, "E180", {"start": v(-2.42, 46.16) * mm, "end": v(-1.45, 48.05) * mm});
            skLineSegment(sketch, "E181", {"start": v(-1.45, 48.05) * mm, "end": v(0, 46.23) * mm});
            skLineSegment(sketch, "E182", {"start": v(0, 46.23) * mm, "end": v(1.07, 48.06) * mm});
            skLineSegment(sketch, "E183", {"start": v(1.07, 48.06) * mm, "end": v(2.42, 46.16) * mm});
            skLineSegment(sketch, "E184", {"start": v(2.42, 46.16) * mm, "end": v(3.58, 47.93) * mm});
            skLineSegment(sketch, "E185", {"start": v(3.56, 48.06) * mm, "end": v(4.83, 45.97) * mm});
            skLineSegment(sketch, "E186", {"start": v(4.83, 45.97) * mm, "end": v(3.58, 47.93) * mm});
            skLineSegment(sketch, "E187", {"start": v(4.83, 45.97) * mm, "end": v(6.08, 47.68) * mm});
            skLineSegment(sketch, "E188", {"start": v(6.08, 47.68) * mm, "end": v(7.23, 45.66) * mm});
            skLineSegment(sketch, "E189", {"start": v(7.23, 45.66) * mm, "end": v(8.57, 47.3) * mm});
            skLineSegment(sketch, "E190", {"start": v(8.57, 47.3) * mm, "end": v(9.61, 45.22) * mm});
            skLineSegment(sketch, "E191", {"start": v(9.61, 45.22) * mm, "end": v(11.04, 46.78) * mm});
            skLineSegment(sketch, "E192", {"start": v(11.04, 46.78) * mm, "end": v(11.96, 44.65) * mm});
            skLineSegment(sketch, "E193", {"start": v(11.96, 44.65) * mm, "end": v(13.47, 46.14) * mm});
            skLineSegment(sketch, "E194", {"start": v(13.47, 46.14) * mm, "end": v(14.29, 43.97) * mm});
            skLineSegment(sketch, "E195", {"start": v(14.29, 43.97) * mm, "end": v(15.86, 45.37) * mm});
            skLineSegment(sketch, "E196", {"start": v(15.86, 45.37) * mm, "end": v(16.57, 43.16) * mm});
            skLineSegment(sketch, "E197", {"start": v(16.57, 43.16) * mm, "end": v(18.22, 44.48) * mm});
            skLineSegment(sketch, "E198", {"start": v(18.22, 44.48) * mm, "end": v(18.8, 42.23) * mm});
            skLineSegment(sketch, "E199", {"start": v(18.8, 42.23) * mm, "end": v(20.52, 43.47) * mm});
            skLineSegment(sketch, "E200", {"start": v(20.99, 41.19) * mm, "end": v(20.52, 43.47) * mm});
            skLineSegment(sketch, "E201", {"start": v(20.99, 41.19) * mm, "end": v(22.77, 42.33) * mm});
            skLineSegment(sketch, "E202", {"start": v(22.77, 42.33) * mm, "end": v(23.11, 40.03) * mm});
            skLineSegment(sketch, "E203", {"start": v(23.11, 40.03) * mm, "end": v(24.95, 41.08) * mm});
            skLineSegment(sketch, "E204", {"start": v(24.95, 41.08) * mm, "end": v(25.18, 38.77) * mm});
            skLineSegment(sketch, "E205", {"start": v(25.18, 38.77) * mm, "end": v(27.07, 39.72) * mm});
            skLineSegment(sketch, "E206", {"start": v(27.07, 39.72) * mm, "end": v(27.17, 37.4) * mm});
            skLineSegment(sketch, "E207", {"start": v(27.17, 37.4) * mm, "end": v(29.1, 38.25) * mm});
            skLineSegment(sketch, "E208", {"start": v(29.1, 38.25) * mm, "end": v(29.1, 35.93) * mm});
            skLineSegment(sketch, "E209", {"start": v(29.1, 35.93) * mm, "end": v(31.07, 36.68) * mm});
            skLineSegment(sketch, "E210", {"start": v(31.07, 36.68) * mm, "end": v(30.93, 34.35) * mm});
            skLineSegment(sketch, "E211", {"start": v(30.93, 34.35) * mm, "end": v(32.95, 35) * mm});
            skLineSegment(sketch, "E212", {"start": v(32.95, 35) * mm, "end": v(32.69, 32.69) * mm});
            skLineSegment(sketch, "E213", {"start": v(32.69, 32.69) * mm, "end": v(34.74, 33.23) * mm});
            skLineSegment(sketch, "E214", {"start": v(34.74, 33.23) * mm, "end": v(34.35, 30.93) * mm});
            skLineSegment(sketch, "E215", {"start": v(34.35, 30.93) * mm, "end": v(36.43, 31.36) * mm});
            skLineSegment(sketch, "E216", {"start": v(36.43, 31.36) * mm, "end": v(35.93, 29.1) * mm});
            skLineSegment(sketch, "E217", {"start": v(35.93, 29.1) * mm, "end": v(38.02, 29.41) * mm});
            skLineSegment(sketch, "E218", {"start": v(38.02, 29.41) * mm, "end": v(37.4, 27.17) * mm});
            skLineSegment(sketch, "E219", {"start": v(37.4, 27.17) * mm, "end": v(39.5, 27.38) * mm});
            skLineSegment(sketch, "E220", {"start": v(39.5, 27.38) * mm, "end": v(38.77, 25.18) * mm});
            skLineSegment(sketch, "E221", {"start": v(38.77, 25.18) * mm, "end": v(40.88, 25.28) * mm});
            skLineSegment(sketch, "E222", {"start": v(40.88, 25.28) * mm, "end": v(40.03, 23.11) * mm});
            skLineSegment(sketch, "E223", {"start": v(40.03, 23.11) * mm, "end": v(42.15, 23.1) * mm});
            skLineSegment(sketch, "E224", {"start": v(42.15, 23.1) * mm, "end": v(41.19, 20.99) * mm});
            skLineSegment(sketch, "E225", {"start": v(41.19, 20.99) * mm, "end": v(43.3, 20.87) * mm});
            skLineSegment(sketch, "E226", {"start": v(43.3, 20.87) * mm, "end": v(42.23, 18.8) * mm});
            skLineSegment(sketch, "E227", {"start": v(42.23, 18.8) * mm, "end": v(44.34, 18.57) * mm});
            skLineSegment(sketch, "E228", {"start": v(44.34, 18.57) * mm, "end": v(43.16, 16.57) * mm});
            skLineSegment(sketch, "E229", {"start": v(43.16, 16.57) * mm, "end": v(45.25, 16.23) * mm});
            skLineSegment(sketch, "E230", {"start": v(45.25, 16.23) * mm, "end": v(43.97, 14.29) * mm});
            skLineSegment(sketch, "E231", {"start": v(43.97, 14.29) * mm, "end": v(46.03, 13.84) * mm});
            skLineSegment(sketch, "E232", {"start": v(46.03, 13.84) * mm, "end": v(44.65, 11.96) * mm});
            skLineSegment(sketch, "E233", {"start": v(44.65, 11.96) * mm, "end": v(46.7, 11.4) * mm});
            skLineSegment(sketch, "E234", {"start": v(46.7, 11.4) * mm, "end": v(45.22, 9.61) * mm});
            skLineSegment(sketch, "E235", {"start": v(45.22, 9.61) * mm, "end": v(47.23, 8.95) * mm});
            skLineSegment(sketch, "E236", {"start": v(47.23, 8.95) * mm, "end": v(45.66, 7.23) * mm});
            skLineSegment(sketch, "E237", {"start": v(45.66, 7.23) * mm, "end": v(47.63, 6.46) * mm});
            skLineSegment(sketch, "E238", {"start": v(47.63, 6.46) * mm, "end": v(45.97, 4.83) * mm});
            skLineSegment(sketch, "E239", {"start": v(45.97, 4.83) * mm, "end": v(47.9, 3.96) * mm});
            skLineSegment(sketch, "E240", {"start": v(47.9, 3.96) * mm, "end": v(46.16, 2.42) * mm});
            skLineSegment(sketch, "E241", {"start": v(46.16, 2.42) * mm, "end": v(48.05, 1.45) * mm});
            skLineSegment(sketch, "E242", {"start": v(48.05, 1.45) * mm, "end": v(46.23, 0) * mm});
            skLineSegment(sketch, "E243", {"start": v(46.23, 0) * mm, "end": v(48.06, -1.07) * mm});
            skLineSegment(sketch, "E244", {"start": v(48.06, -1.07) * mm, "end": v(46.16, -2.42) * mm});
            skLineSegment(sketch, "E245", {"start": v(46.16, -2.42) * mm, "end": v(47.93, -3.58) * mm});
            skLineSegment(sketch, "E246", {"start": v(47.93, -3.58) * mm, "end": v(45.97, -4.83) * mm});
            skLineSegment(sketch, "E247", {"start": v(45.97, -4.83) * mm, "end": v(47.68, -6.08) * mm});
            skLineSegment(sketch, "E248", {"start": v(47.68, -6.08) * mm, "end": v(45.66, -7.23) * mm});
            skLineSegment(sketch, "E249", {"start": v(45.7, -7.28) * mm, "end": v(47.3, -8.57) * mm});
            skLineSegment(sketch, "E250", {"start": v(47.3, -8.57) * mm, "end": v(45.22, -9.61) * mm});
            skLineSegment(sketch, "E251", {"start": v(45.66, -7.23) * mm, "end": v(47.3, -8.57) * mm});
            skLineSegment(sketch, "E252", {"start": v(45.22, -9.61) * mm, "end": v(46.78, -11.04) * mm});
            skLineSegment(sketch, "E253", {"start": v(44.65, -11.96) * mm, "end": v(46.78, -11.04) * mm});
            skLineSegment(sketch, "E254", {"start": v(44.65, -11.96) * mm, "end": v(46.14, -13.47) * mm});
            skLineSegment(sketch, "E255", {"start": v(46.14, -13.47) * mm, "end": v(43.97, -14.29) * mm});
            skLineSegment(sketch, "E256", {"start": v(43.97, -14.29) * mm, "end": v(45.37, -15.86) * mm});
            skLineSegment(sketch, "E257", {"start": v(45.37, -15.86) * mm, "end": v(43.16, -16.57) * mm});
            skLineSegment(sketch, "E258", {"start": v(43.16, -16.57) * mm, "end": v(44.48, -18.22) * mm});
            skLineSegment(sketch, "E259", {"start": v(44.48, -18.22) * mm, "end": v(42.23, -18.8) * mm});
            skLineSegment(sketch, "E260", {"start": v(42.23, -18.8) * mm, "end": v(43.47, -20.52) * mm});
            skLineSegment(sketch, "E261", {"start": v(43.47, -20.52) * mm, "end": v(41.19, -20.99) * mm});
            skLineSegment(sketch, "E262", {"start": v(41.19, -20.99) * mm, "end": v(42.33, -22.77) * mm});
            skLineSegment(sketch, "E263", {"start": v(38.25, -29.1) * mm, "end": v(37.4, -27.17) * mm});
            skLineSegment(sketch, "E264", {"start": v(37.4, -27.17) * mm, "end": v(39.72, -27.07) * mm});
            skLineSegment(sketch, "E265", {"start": v(39.72, -27.07) * mm, "end": v(38.77, -25.18) * mm});
            skLineSegment(sketch, "E266", {"start": v(38.77, -25.18) * mm, "end": v(41.08, -24.95) * mm});
            skLineSegment(sketch, "E267", {"start": v(41.08, -24.95) * mm, "end": v(40.03, -23.11) * mm});
            skLineSegment(sketch, "E268", {"start": v(40.03, -23.11) * mm, "end": v(42.33, -22.77) * mm});
            skSolve(sketch);
        }
        {
            var Q0;
            Q0 = qSketchRegion(id + "F0", true);
            extrude(context, id + "F1", {"entities" : qUnion([Q0]), "depth" : 6.1 * mm});
        }
        {
            var Q0;
            Q0=sQuery(id+"F0.wireOp",VERTEX,"E1");
            var Q1;
            Q1=sQuery(id+"F0.wireOp",VERTEX,"E2.1.0");
            var Q2;
            Q2=sQuery(id+"F0.wireOp",VERTEX,"E2.2.0");
            var Q3;
            Q3=sQuery(id+"F0.wireOp",VERTEX,"E2.3.0");
            var Q4;
            Q4=sQuery(id+"F0.wireOp",VERTEX,"E2.4.0");
            var Q5;
            Q5=sQuery(id+"F0.wireOp",VERTEX,"E2.5.0");
            var Q6;
            Q6=sQuery(id+"F0.wireOp",VERTEX,"E2.6.0");
            var Q7;
            Q7=sQuery(id+"F0.wireOp",VERTEX,"E2.7.0");
            var Q8;
            Q8=makeQuery(id+"F1.opExtrude","SWEPT_BODY",BODY,{"disambiguationData":[OSD([sQuery(id+"F0.wireOp",EDGE,"E0")])]});
            hole(context, id + "F2", {"style" : HoleStyle.SIMPLE, "endStyle" : HoleEndStyle.THROUGH, "oppositeDirection" : true, "holeDiameter" : 6.35 * mm, "isTappedThrough" : true, "tappedDepth" : 12.7 * mm, "tapClearance" : 3, "locations" : qUnion([Q0, Q1, Q2, Q3, Q4, Q5, Q6, Q7]), "scope" : qUnion([Q8])});
        }
        {
            var Q0;
            Q0=sQuery(id+"F0.wireOp",VERTEX,"E4.1.0");
            var Q1;
            Q1=sQuery(id+"F0.wireOp",VERTEX,"E4.2.0");
            var Q2;
            Q2=sQuery(id+"F0.wireOp",VERTEX,"E4.3.0");
            var Q3;
            Q3=sQuery(id+"F0.wireOp",VERTEX,"E3");
            var Q4;
            Q4=sQuery(id+"F0.wireOp",VERTEX,"E0.center");
            var Q5;
            Q5=makeQuery(id+"F1.opExtrude","SWEPT_BODY",BODY,{"disambiguationData":[OSD([sQuery(id+"F0.wireOp",EDGE,"E0")])]});
            hole(context, id + "F3", {"style" : HoleStyle.SIMPLE, "endStyle" : HoleEndStyle.THROUGH, "oppositeDirection" : true, "holeDiameter" : 3.17 * mm, "isTappedThrough" : true, "tappedDepth" : 12.7 * mm, "tapClearance" : 3, "locations" : qUnion([Q0, Q1, Q2, Q3, Q4]), "scope" : qUnion([Q5])});
        }
        {
            var Q0;
            Q0=sQuery(id+"F0.wireOp",VERTEX,"E0.center");
            var Q1;
            Q1=makeQuery(id+"F1.opExtrude","SWEPT_BODY",BODY,{"disambiguationData":[OSD([sQuery(id+"F0.wireOp",EDGE,"E0")])]});
            hole(context, id + "F4", {"style" : HoleStyle.SIMPLE, "endStyle" : HoleEndStyle.THROUGH, "oppositeDirection" : true, "holeDiameter" : 6.35 * mm, "isTappedThrough" : true, "tappedDepth" : 12.7 * mm, "tapClearance" : 3, "locations" : qUnion([Q0]), "scope" : qUnion([Q1])});
        }
    });
